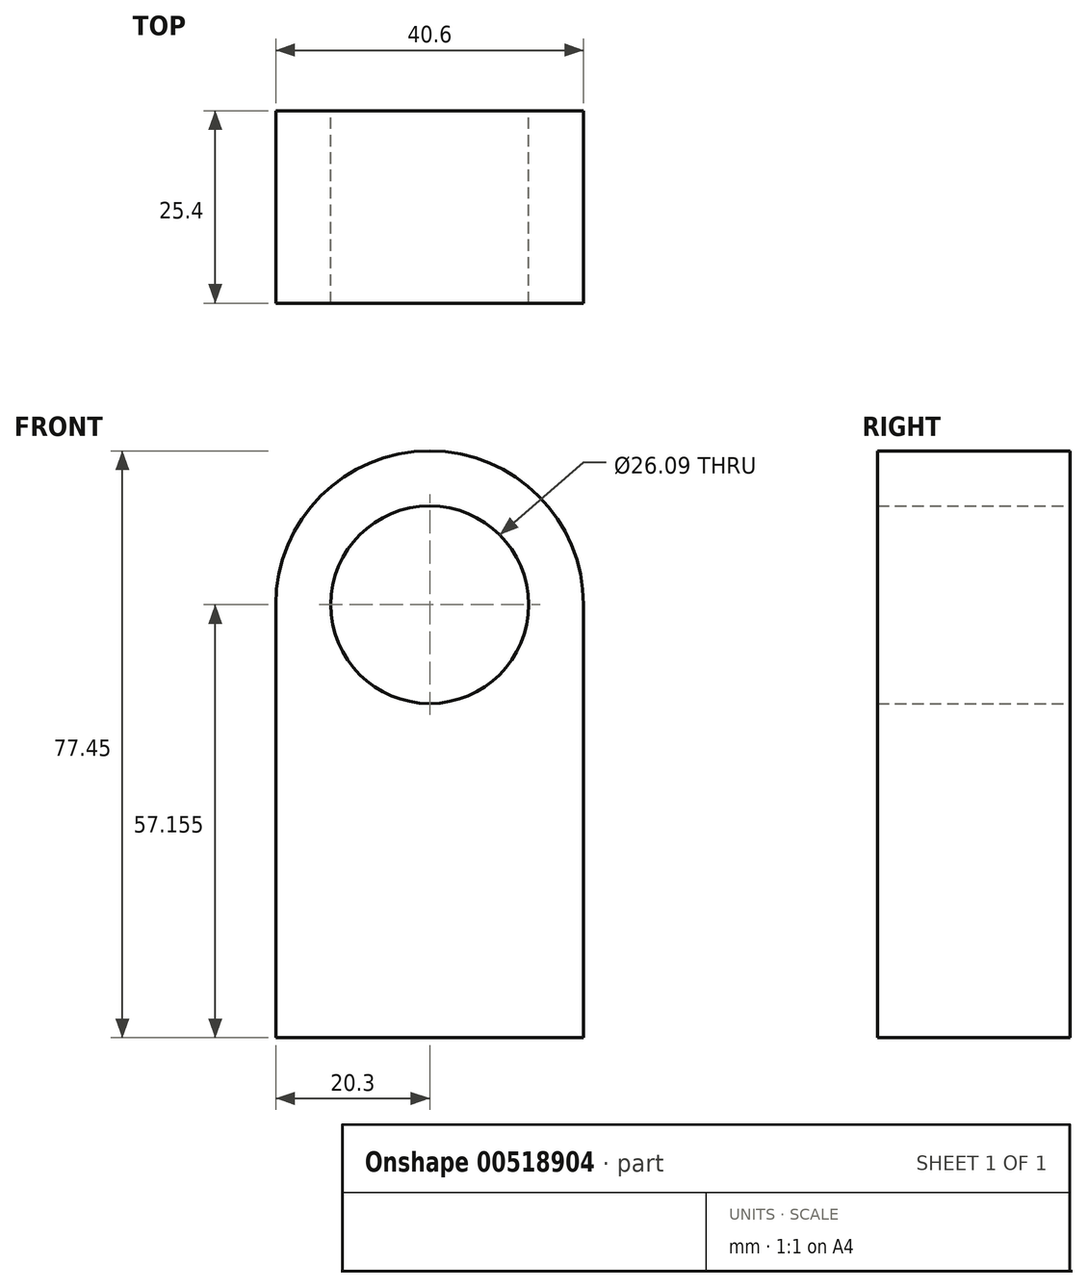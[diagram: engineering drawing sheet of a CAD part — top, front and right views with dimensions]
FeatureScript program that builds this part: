
annotation { "Feature Type Name" : "Feature", "Feature Type Description" : "" }
export const myFeature = defineFeature(function(context is Context, id is Id, definition is map)
    precondition{}
    {
        {
            var Q0;
            Q0=qCreatedBy(makeId("Front.planeOp"),FACE);
            var sketch = newSketch(context, id + "F0", { "sketchPlane" : qUnion([Q0])});
            skLineSegment(sketch, "E0.bottom", {"start": v(-20.3, 28.58) * mm, "end": v(20.3, 28.58) * mm});
            skLineSegment(sketch, "E0.top", {"start": v(-20.3, -28.58) * mm, "end": v(20.3, -28.58) * mm});
            skLineSegment(sketch, "E0.left", {"start": v(-20.3, 28.58) * mm, "end": v(-20.3, -28.58) * mm});
            skLineSegment(sketch, "E0.right", {"start": v(20.3, 28.58) * mm, "end": v(20.3, -28.58) * mm});
            skPoint(sketch, "E0.middle", {"position": v(0, 0) * mm});
            skArc(sketch, "E1", {"start": v(20.3, 28.58) * mm, "mid": v(0, 48.87) * mm, "end": v(-20.3, 28.58) * mm});
            skCircle(sketch, "E2", {"center": v(0, 28.58) * mm, "radius": 13.04 * mm});
            skSolve(sketch);
        }
        {
            var Q0;
            Q0 = qSketchRegion(id + "F0", true);
            extrude(context, id + "F1", {"entities" : qUnion([Q0]), "depth" : 25.4 * mm, "offsetDistance" : 25.4 * mm});
        }
    });
